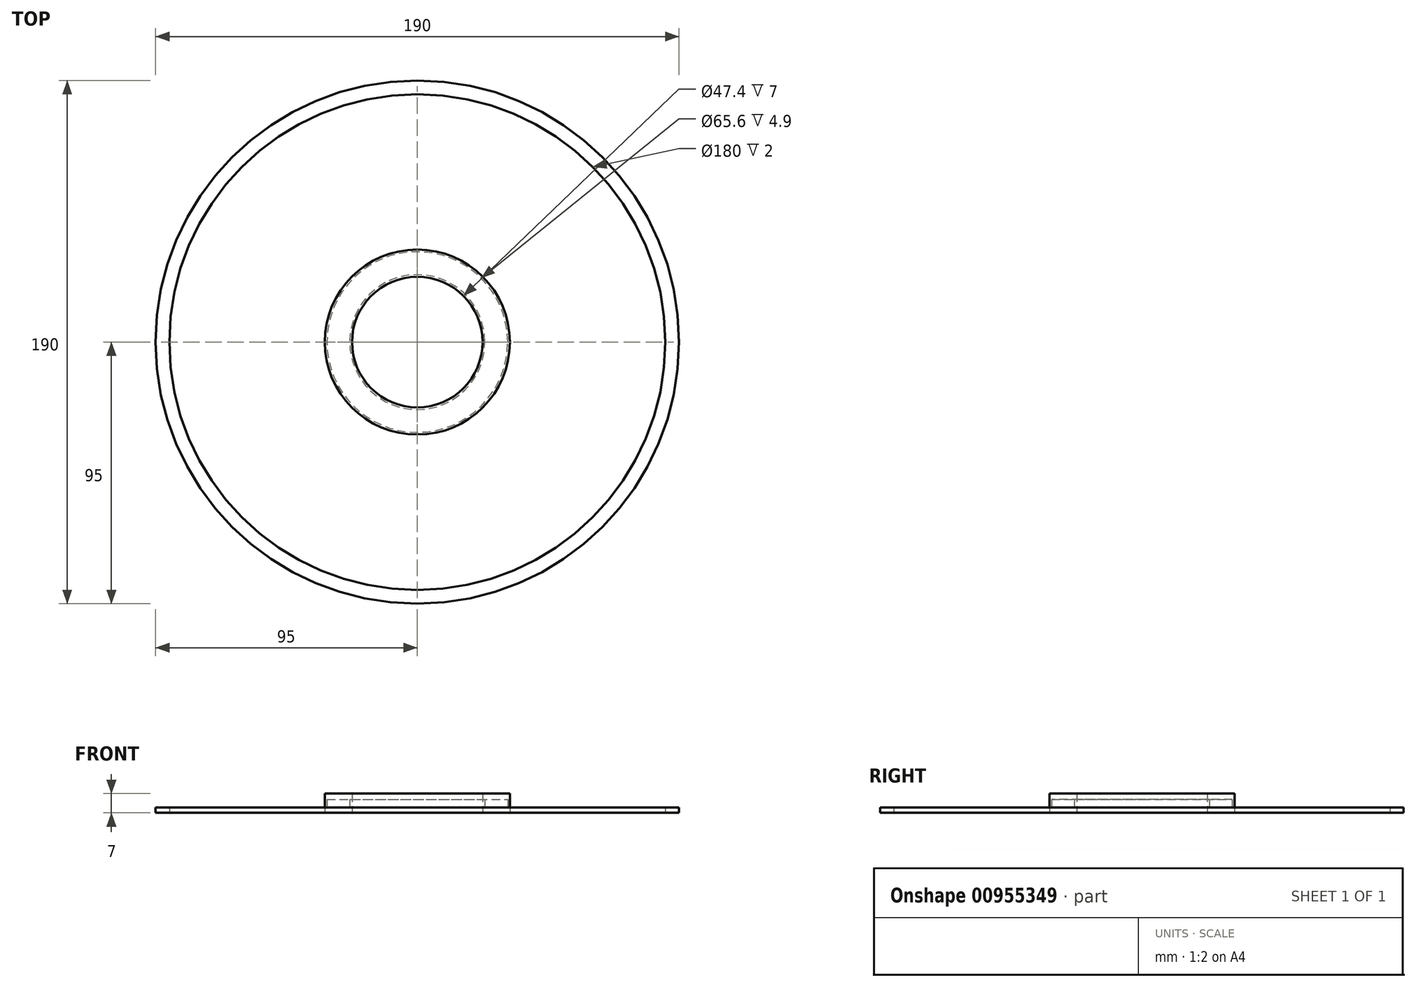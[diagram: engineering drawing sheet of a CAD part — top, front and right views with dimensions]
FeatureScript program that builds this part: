
annotation { "Feature Type Name" : "Feature", "Feature Type Description" : "" }
export const myFeature = defineFeature(function(context is Context, id is Id, definition is map)
    precondition{}
    {
        {
            var Q0;
            Q0=qCreatedBy(makeId("Top.planeOp"),FACE);
            var sketch = newSketch(context, id + "F0", { "sketchPlane" : qUnion([Q0])});
            skCircle(sketch, "E0", {"center": v(0, 0) * mm, "radius": 95 * mm});
            skCircle(sketch, "E1", {"center": v(0, 0) * mm, "radius": 90 * mm});
            skCircle(sketch, "E2", {"center": v(0, 0) * mm, "radius": 33.6 * mm});
            skCircle(sketch, "E3", {"center": v(0, 0) * mm, "radius": 23.7 * mm});
            skSolve(sketch);
        }
        {
            var Q0;
            Q0=makeQuery(id+"F0.imprint","IMPRINT",FACE,{"disambiguationData":[TD([[makeQuery(id+"F0.imprint","IMPRINT",EDGE,{"derivedFrom":sQuery(id+"F0.wireOp",EDGE,"E0")}),1.0]])]});
            var Q1;
            Q1=sQuery(id+"F0.wireOp",EDGE,"E1");
            var Q2;
            Q2=sQuery(id+"F0.wireOp",EDGE,"E0");
            extrude(context, id + "F1", {"entities" : qUnion([Q0]), "surfaceEntities" : qUnion([Q1, Q2]), "depth" : 2 * mm, "offsetDistance" : 25 * mm});
        }
        {
            var Q0;
            Q0=makeQuery(id+"F0.imprint","IMPRINT",FACE,{"disambiguationData":[TD([[makeQuery(id+"F0.imprint","IMPRINT",EDGE,{"derivedFrom":sQuery(id+"F0.wireOp",EDGE,"E2")}),1.0]])]});
            var Q1;
            Q1=sQuery(id+"F0.wireOp",EDGE,"E2");
            extrude(context, id + "F2", {"entities" : qUnion([Q0]), "surfaceEntities" : qUnion([Q1]), "depth" : 7 * mm, "offsetDistance" : 25 * mm});
        }
        {
            var Q0;
            Q0=makeQuery(id+"F2.opExtrude","CAP_FACE",FACE,{"disambiguationData":[OSD([sQuery(id+"F0.wireOp",EDGE,"E2"),sQuery(id+"F0.wireOp",EDGE,"E3")])],"isStart":true});
            var sketch = newSketch(context, id + "F3", { "sketchPlane" : qUnion([Q0])});
            skCircle(sketch, "E4", {"center": v(0, 0) * mm, "radius": 24.5 * mm});
            skCircle(sketch, "E5", {"center": v(0, 0) * mm, "radius": 32.8 * mm});
            skSolve(sketch);
        }
        {
            var Q0;
            Q0 = qSketchRegion(id + "F3", true);
            extrude(context, id + "F4", {"entities" : qUnion([Q0]), "operationType" : NewBodyOperationType.REMOVE, "oppositeDirection" : true, "depth" : 4.9 * mm, "offsetDistance" : 25 * mm});
        }
    });
